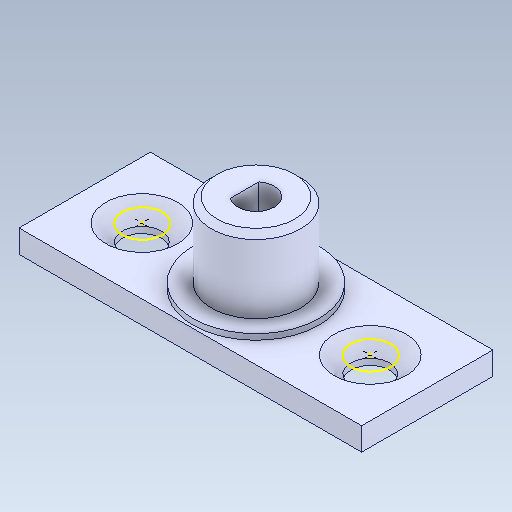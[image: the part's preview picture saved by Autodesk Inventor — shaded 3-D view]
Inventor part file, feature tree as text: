
AUTODESK INVENTOR PART (.ipt)
format: ipt  version: 2021 (Build 250183000, 183)  size: 169,984 bytes
history: mixed  units: in
note: dims shown in document units (in); Inventor stores cm internally (conversion verified against a paired STEP export)
features: sketch x5, extrude x3, other x3, reference x2, chamfer x1, hole x1, projected_geometry x1, imported_body x1
ambient origin geometry x8: Origin, YZ Plane, XZ Plane, XY Plane, X Axis, Y Axis, Z Axis, Center Point
bodies: Solid1 (imported_parasolid)
feature tree (17):
  extrude  "Extrusion1"  Depth=0.3937in TaperAngle=0.0deg
  extrude  "Extrusion2"  Depth=0.3937in TaperAngle=0.0deg
  extrude  "Extrusion3"  Depth=0.0787in
  chamfer  "Chamfer1"  [1 undecoded]
  sketch  "Sketch4"  dims[d19=0.1339in d20=0.2362in d21=0.248in d22=0.0787in d23=90.0deg d24=0.315in d25=0.0in]
  hole  "Hole2"  [1 undecoded]
  sketch  "Sketch1"  dims[d1=0.3937in d2=0.0in d3=0.3937in d4=0.0in]
  projected_geometry  "Projected Loop1"
  sketch  "Sketch2"  dims[d5=0.0039in d6=0.3937in d7=0.0in]
  sketch  "Sketch3"  dims[d8=0.0197in d9=0.0787in d10=45.0deg d18=0.0039in]
  reference  "Reference1"
  reference  "Reference2"
  sketch  "Sketch6"
  other  "CSK for M4 Countersunk Flat Head Screw1"
  other  "sub_assy_robot_arm_link1.iam"
  other  "arm_1_v2:1"
  imported_body  NMx_Import_Brep_tag  [imported B-rep: ~18 faces, bbox_mm=[30.0, 9.0, 11.5]]
note: 2 required parameter values undecoded (feature->parameter linkage not recoverable at this tier; creation-order binding heuristic only, values carry confidence <= 0.55)
